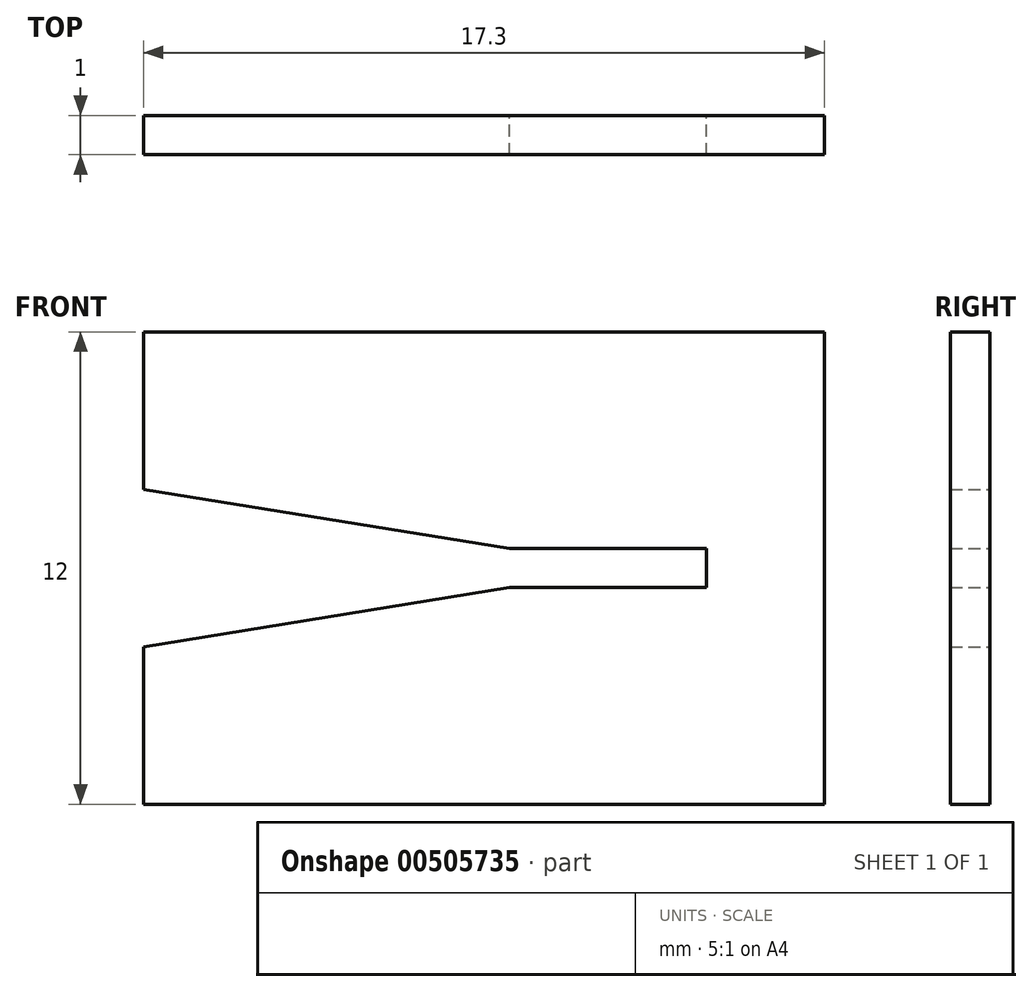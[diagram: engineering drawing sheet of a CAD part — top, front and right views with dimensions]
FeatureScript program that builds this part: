
annotation { "Feature Type Name" : "Feature", "Feature Type Description" : "" }
export const myFeature = defineFeature(function(context is Context, id is Id, definition is map)
    precondition{}
    {
        {
            var Q0;
            Q0=qCreatedBy(makeId("Front.planeOp"),FACE);
            var sketch = newSketch(context, id + "F0", { "sketchPlane" : qUnion([Q0])});
            skLineSegment(sketch, "E0", {"start": v(-17.3, 6) * mm, "end": v(0, 6) * mm});
            skLineSegment(sketch, "E1", {"start": v(0, 6) * mm, "end": v(0, -6) * mm});
            skLineSegment(sketch, "E2", {"start": v(0, -6) * mm, "end": v(-17.3, -6) * mm});
            skLineSegment(sketch, "E3", {"start": v(-17.3, -6) * mm, "end": v(-17.3, -2) * mm});
            skLineSegment(sketch, "E4", {"start": v(-17.3, -2) * mm, "end": v(-8, -0.5) * mm});
            skLineSegment(sketch, "E5", {"start": v(-8, -0.5) * mm, "end": v(-3, -0.5) * mm});
            skLineSegment(sketch, "E6", {"start": v(-3, -0.5) * mm, "end": v(-3, 0.5) * mm});
            skLineSegment(sketch, "E7", {"start": v(-3, 0.5) * mm, "end": v(-8, 0.5) * mm});
            skLineSegment(sketch, "E8", {"start": v(-8, 0.5) * mm, "end": v(-17.3, 2) * mm});
            skLineSegment(sketch, "E9", {"start": v(-17.3, 2) * mm, "end": v(-17.3, 6) * mm});
            skSolve(sketch);
        }
        {
            var Q0;
            Q0 = qSketchRegion(id + "F0", true);
            extrude(context, id + "F1", {"entities" : qUnion([Q0]), "depth" : 1 * mm});
        }
    });
